# Revit family: Cover_Access_Plug-Zurn-Z1468
name_source: partatom
category: Plumbing Fixtures
units: mm (PartAtom-declared; Revit-internal decimal feet)

## family parameters
Cut with Voids When Loaded = No
Host = Face
Maintain Annotation Orientation = No
OmniClass Number = 23.60.30.11.14
OmniClass Title = Pipework Fittings
Part Type = Normal
Room Calculation Point = No
Round Connector Dimension = Use Radius
Shared = No

## types (20) — shared parameters
Assembly Code = D2030100
Body Depth = 1.75 "
CW Connection = No
Default Elevation = 20 "
Description = ACCESS COVER AND PLUG
HW Connection = No
Main Material = Bronze - Zurn - Polished
Manufacturer = Zurn Water, LLC
Manufacurer Brand = Zurn
Modified Date = 12/30/2025
Product Documentation Link = https://files.zurn.com
Product Page URL = https://www.zurn.com
Product data url = https://www.bimobject.com
URL = www.zurn.com
Vent Connection = No
WFU = 1
Waste Connection = Yes
zero-valued in all types: CWFU, HWFU

## per-type parameters (varying)
| type | Approx. Weight (Lbs) | B Dimension | Connector Radius | Model | Pipe Size_A Inside Diameter | Pipe Size_A Nominal Diameter | Pipe Size_A Outer Diameter | Plate Material | Type Comments |
| ZAB1468-4 | 8 " | 7 " | 2 " | ZAB1464 | 4.026 " | 4 " | 4.5 " | Bronze - Zurn - Polished | ZAB1464-4 Inch Plug |
| ZAB1468-3 | 5 " | 5 " | 1.5 " | ZAB1464 | 3.068 " | 3 " | 3.5 " | Bronze - Zurn - Polished | ZAB1464-3 Inch Plug |
| ZAB1468-3.5 | 6 " | 5 " | 1.75 " | ZAB1464 | 3.468 " | 3.5 " | 4 " | Bronze - Zurn - Polished | ZAB1464-3.5 Inch Plug |
| ZAB1468-5 | 11 " | 7 " | 2.5 " | ZAB1464 | 5.047 " | 5 " | 5.563 " | Bronze - Zurn - Polished | ZAB1464-5 Inch Plug |
| ZAB1468-6 | 14 " | 9 " | 3 " | ZAB1464 | 6.065 " | 6 " | 6.625 " | Bronze - Zurn - Polished | ZAB1464-6 Inch Plug |
| ZAB1468-8 | 25 " | 11 " | 4 " | ZAB1464 | 7.981 " | 8 " | 8.625 " | Bronze - Zurn - Polished | ZAB1464-8 Inch Plug |
| ZAB1468-2 | 5 " | 5 " | 1 " | ZAB1464 | 2.067 " | 2 " | 2.375 " | Bronze - Zurn - Polished | ZAB1464-2 Inch Plug |
| ZAB1468-2.5 | 5 " | 5 " | 1.25 " | ZAB1464 | 2.469 " | 2.5 " | 2.875 " | Bronze - Zurn - Polished | ZAB1464-2.5 Inch Plug |
| ZAB1468-1.25 | 4 " | 4 " | 0.625 " | ZAB1464 | 0.364 " | 1.25 " | 0.54 " | Bronze - Zurn - Polished | ZAB1464-1.25 Inch Plug |
| ZAB1468-1.5 | 4 " | 4 " | 0.25 " | ZAB1464 | 0.622 " | 0.5 " | 0.84 " | Bronze - Zurn - Polished | ZAB1464-1.5 Inch Plug |
| ZS1468-4 | 8 " | 7 " | 2 " | ZS1468 | 4.026 " | 4 " | 4.5 " | Steel - Zurn - Stainless - Type - 304 | ZS1468-4 Inch Plug |
| ZS1468-3 | 5 " | 5 " | 1.5 " | ZS1468 | 3.068 " | 3 " | 3.5 " | Steel - Zurn - Stainless - Type - 304 | ZS1468-3 Inch Plug |
| ZS1468-3.5 | 6 " | 5 " | 1.75 " | ZS1468 | 3.468 " | 3.5 " | 4 " | Steel - Zurn - Stainless - Type - 304 | ZS1468-3.5 Inch Plug |
| ZS1468-5 | 11 " | 7 " | 2.5 " | ZS1468 | 5.047 " | 5 " | 5.563 " | Steel - Zurn - Stainless - Type - 304 | ZS1468-5 Inch Plug |
| ZS1468-6 | 14 " | 9 " | 3 " | ZS1468 | 6.065 " | 6 " | 6.625 " | Steel - Zurn - Stainless - Type - 304 | ZS1468-6 Inch Plug |
| ZS1468-8 | 25 " | 11 " | 4 " | ZS1468 | 7.981 " | 8 " | 8.625 " | Steel - Zurn - Stainless - Type - 304 | ZS1468-8 Inch Plug |
| ZS1468-2 | 5 " | 5 " | 1 " | ZS1468 | 2.067 " | 2 " | 2.375 " | Steel - Zurn - Stainless - Type - 304 | ZS1468-2 Inch Plug |
| ZS1468-2.5 | 5 " | 5 " | 1.25 " | ZS1468 | 2.469 " | 2.5 " | 2.875 " | Steel - Zurn - Stainless - Type - 304 | ZS1468-2.5 Inch Plug |
| ZS1468-1.25 | 4 " | 4 " | 0.625 " | ZS1468 | 0.364 " | 1.25 " | 0.54 " | Steel - Zurn - Stainless - Type - 304 | ZS1468-1.25 Inch Plug |
| ZS1468-1.5 | 4 " | 4 " | 0.25 " | ZS1468 | 0.622 " | 0.5 " | 0.84 " | Steel - Zurn - Stainless - Type - 304 | ZS1468-1.5 Inch Plug |

## geometry (parser evidence)
native form markers: Blend x14, Sweep x2
no freeform markers — native parametric forms only
